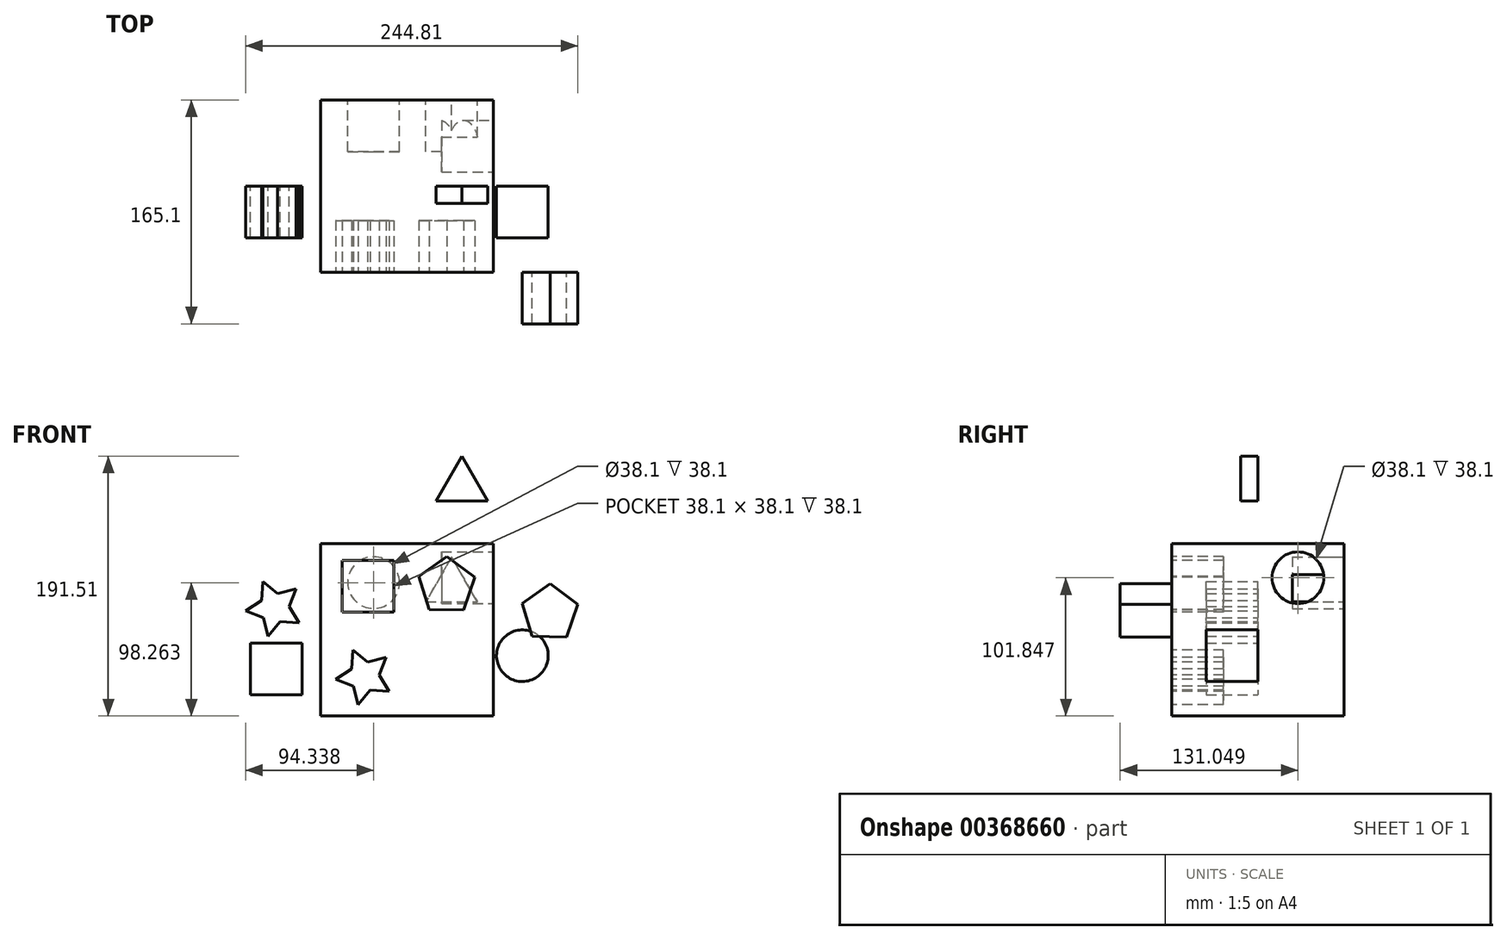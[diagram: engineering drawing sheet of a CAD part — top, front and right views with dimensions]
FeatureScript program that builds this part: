
annotation { "Feature Type Name" : "Feature", "Feature Type Description" : "" }
export const myFeature = defineFeature(function(context is Context, id is Id, definition is map)
    precondition{}
    {
        {
            var Q0;
            Q0=qCreatedBy(makeId("Front.planeOp"),FACE);
            var sketch = newSketch(context, id + "F0", { "sketchPlane" : qUnion([Q0])});
            skLineSegment(sketch, "E0.bottom", {"start": v(63.5, 63.5) * mm, "end": v(-63.5, 63.5) * mm});
            skLineSegment(sketch, "E0.top", {"start": v(63.5, -63.5) * mm, "end": v(-63.5, -63.5) * mm});
            skLineSegment(sketch, "E0.left", {"start": v(63.5, 63.5) * mm, "end": v(63.5, -63.5) * mm});
            skLineSegment(sketch, "E0.right", {"start": v(-63.5, 63.5) * mm, "end": v(-63.5, -63.5) * mm});
            skPoint(sketch, "E0.middle", {"position": v(0, 0) * mm});
            skSolve(sketch);
        }
        {
            var Q0;
            Q0 = qSketchRegion(id + "F0", true);
            extrude(context, id + "F1", {"entities" : qUnion([Q0]), "endBound" : BoundingType.SYMMETRIC, "depth" : 127 * mm});
        }
        {
            var Q0;
            Q0=makeQuery(id+"F1.opExtrude","CAP_FACE",FACE,{"disambiguationData":[OSD([sQuery(id+"F0.wireOp",EDGE,"E0.bottom"),sQuery(id+"F0.wireOp",EDGE,"E0.top"),sQuery(id+"F0.wireOp",EDGE,"E0.left"),sQuery(id+"F0.wireOp",EDGE,"E0.right")])],"isStart":false});
            var sketch = newSketch(context, id + "F2", { "sketchPlane" : qUnion([Q0])});
            skLineSegment(sketch, "E1.bottom", {"start": v(-47.79, 51.24) * mm, "end": v(-9.69, 51.24) * mm});
            skLineSegment(sketch, "E1.top", {"start": v(-47.79, 13.14) * mm, "end": v(-9.69, 13.14) * mm});
            skLineSegment(sketch, "E1.left", {"start": v(-47.79, 51.24) * mm, "end": v(-47.79, 13.14) * mm});
            skLineSegment(sketch, "E1.right", {"start": v(-9.69, 51.24) * mm, "end": v(-9.69, 13.14) * mm});
            skLineSegment(sketch, "E2.bottom", {"start": v(67.2, 12.11) * mm, "end": v(105.3, 12.11) * mm});
            skLineSegment(sketch, "E2.top", {"start": v(67.2, -25.99) * mm, "end": v(105.3, -25.99) * mm});
            skLineSegment(sketch, "E2.left", {"start": v(67.2, 12.11) * mm, "end": v(67.2, -25.99) * mm});
            skLineSegment(sketch, "E2.right", {"start": v(105.3, 12.11) * mm, "end": v(105.3, -25.99) * mm});
            skSolve(sketch);
        }
        {
            var Q0;
            Q0 = qSketchRegion(id + "F2", true);
            extrude(context, id + "F3", {"entities" : qUnion([Q0]), "operationType" : NewBodyOperationType.REMOVE, "oppositeDirection" : true, "depth" : 38.1 * mm});
        }
        {
            var Q0;
            Q0=makeQuery(id+"F1.opExtrude","CAP_FACE",FACE,{"disambiguationData":[OSD([sQuery(id+"F0.wireOp",EDGE,"E0.bottom"),sQuery(id+"F0.wireOp",EDGE,"E0.top"),sQuery(id+"F0.wireOp",EDGE,"E0.left"),sQuery(id+"F0.wireOp",EDGE,"E0.right")])],"isStart":false});
            var sketch = newSketch(context, id + "F4", { "sketchPlane" : qUnion([Q0])});
            skCircle(sketch, "E3.cCircle", {"center": v(29.22, 32.27) * mm, "radius": 17.48 * mm, "construction": true});
            skLineSegment(sketch, "E3.0", {"start": v(16.28, 14.97) * mm, "end": v(8.76, 39.23) * mm});
            skLineSegment(sketch, "E3.1", {"start": v(8.76, 39.23) * mm, "end": v(29.52, 53.88) * mm});
            skLineSegment(sketch, "E3.2", {"start": v(29.52, 53.88) * mm, "end": v(49.86, 38.66) * mm});
            skLineSegment(sketch, "E3.3", {"start": v(49.86, 38.66) * mm, "end": v(41.67, 14.62) * mm});
            skLineSegment(sketch, "E3.4", {"start": v(41.67, 14.62) * mm, "end": v(16.28, 14.97) * mm});
            skPoint(sketch, "E3.0.midPoint", {"position": v(12.52, 27.1) * mm});
            skSolve(sketch);
        }
        {
            var Q0;
            Q0 = qSketchRegion(id + "F4", true);
            extrude(context, id + "F5", {"entities" : qUnion([Q0]), "operationType" : NewBodyOperationType.REMOVE, "oppositeDirection" : true, "depth" : 38.1 * mm});
        }
        {
            var Q0;
            Q0=makeQuery(id+"F1.opExtrude","CAP_FACE",FACE,{"disambiguationData":[OSD([sQuery(id+"F0.wireOp",EDGE,"E0.bottom"),sQuery(id+"F0.wireOp",EDGE,"E0.top"),sQuery(id+"F0.wireOp",EDGE,"E0.left"),sQuery(id+"F0.wireOp",EDGE,"E0.right")])],"isStart":true});
            var sketch = newSketch(context, id + "F6", { "sketchPlane" : qUnion([Q0])});
            skCircle(sketch, "E4.cCircle", {"center": v(-32.84, 31.52) * mm, "radius": 11 * mm, "construction": true});
            skLineSegment(sketch, "E4.0", {"start": v(-13.8, 20.52) * mm, "end": v(-51.9, 20.52) * mm});
            skLineSegment(sketch, "E4.1", {"start": v(-51.9, 20.52) * mm, "end": v(-32.84, 53.52) * mm});
            skLineSegment(sketch, "E4.2", {"start": v(-32.84, 53.52) * mm, "end": v(-13.8, 20.52) * mm});
            skPoint(sketch, "E4.0.midPoint", {"position": v(-32.84, 20.52) * mm});
            skSolve(sketch);
        }
        {
            var Q0;
            Q0 = qSketchRegion(id + "F6", true);
            extrude(context, id + "F7", {"entities" : qUnion([Q0]), "operationType" : NewBodyOperationType.REMOVE, "oppositeDirection" : true, "depth" : 38.1 * mm});
        }
        {
            var Q0;
            Q0=makeQuery(id+"F1.opExtrude","CAP_FACE",FACE,{"disambiguationData":[OSD([sQuery(id+"F0.wireOp",EDGE,"E0.bottom"),sQuery(id+"F0.wireOp",EDGE,"E0.top"),sQuery(id+"F0.wireOp",EDGE,"E0.left"),sQuery(id+"F0.wireOp",EDGE,"E0.right")])],"isStart":true});
            var sketch = newSketch(context, id + "F8", { "sketchPlane" : qUnion([Q0])});
            skCircle(sketch, "E5", {"center": v(24.54, 34.76) * mm, "radius": 19.05 * mm});
            skSolve(sketch);
        }
        {
            var Q0;
            Q0 = qSketchRegion(id + "F8", true);
            extrude(context, id + "F9", {"entities" : qUnion([Q0]), "operationType" : NewBodyOperationType.REMOVE, "oppositeDirection" : true, "depth" : 38.1 * mm});
        }
        {
            var Q0;
            Q0=makeQuery(id+"F1.opExtrude","CAP_FACE",FACE,{"disambiguationData":[OSD([sQuery(id+"F0.wireOp",EDGE,"E0.bottom"),sQuery(id+"F0.wireOp",EDGE,"E0.top"),sQuery(id+"F0.wireOp",EDGE,"E0.left"),sQuery(id+"F0.wireOp",EDGE,"E0.right")])],"isStart":false});
            var sketch = newSketch(context, id + "F10", { "sketchPlane" : qUnion([Q0])});
            skPoint(sketch, "E6.0.midPoint", {"position": v(-46.2, -25.61) * mm});
            skLineSegment(sketch, "E7", {"start": v(-40.74, -28.86) * mm, "end": v(-39.78, -14.86) * mm});
            skLineSegment(sketch, "E8", {"start": v(-28.98, -23.83) * mm, "end": v(-39.78, -14.86) * mm});
            skLineSegment(sketch, "E9", {"start": v(-28.98, -23.83) * mm, "end": v(-15.37, -20.41) * mm});
            skLineSegment(sketch, "E10", {"start": v(-15.37, -20.41) * mm, "end": v(-20.56, -33.45) * mm});
            skLineSegment(sketch, "E11", {"start": v(-20.56, -33.45) * mm, "end": v(-13.1, -45.34) * mm});
            skLineSegment(sketch, "E12", {"start": v(-13.1, -45.34) * mm, "end": v(-27.11, -44.43) * mm});
            skLineSegment(sketch, "E13", {"start": v(-27.11, -44.43) * mm, "end": v(-36.12, -55.2) * mm});
            skLineSegment(sketch, "E14", {"start": v(-36.12, -55.2) * mm, "end": v(-39.58, -41.6) * mm});
            skLineSegment(sketch, "E15", {"start": v(-52.6, -36.36) * mm, "end": v(-39.58, -41.6) * mm});
            skLineSegment(sketch, "E16", {"start": v(-40.74, -28.86) * mm, "end": v(-52.6, -36.36) * mm});
            skArc(sketch, "E17.trimOffspring", {"start": v(-17.82, -45.04) * mm, "mid": v(-16.63, -43.2) * mm, "end": v(-15.7, -41.22) * mm, "construction": true});
            skPoint(sketch, "E18.orphan", {"position": v(-36.69, -22.08) * mm});
            skPoint(sketch, "E19.orphan", {"position": v(-44.79, -35.65) * mm});
            skPoint(sketch, "E20.orphan", {"position": v(-34.38, -47.54) * mm});
            skPoint(sketch, "E21.orphan", {"position": v(-19.85, -41.32) * mm});
            skPoint(sketch, "E22.1.end.orphan", {"position": v(-21.28, -25.58) * mm});
            skSolve(sketch);
        }
        {
            var Q0;
            Q0 = qSketchRegion(id + "F10", true);
            extrude(context, id + "F11", {"entities" : qUnion([Q0]), "operationType" : NewBodyOperationType.REMOVE, "oppositeDirection" : true, "depth" : 38.1 * mm});
        }
        {
            var Q0;
            Q0=makeQuery(id+"F1.opExtrude","SWEPT_FACE",FACE,{"disambiguationData":[OSD([sQuery(id+"F0.wireOp",EDGE,"E0.left")])]});
            var sketch = newSketch(context, id + "F12", { "sketchPlane" : qUnion([Q0])});
            skCircle(sketch, "E23", {"center": v(29.45, 38.35) * mm, "radius": 19.05 * mm});
            skSolve(sketch);
        }
        {
            var Q0;
            Q0 = qSketchRegion(id + "F12", true);
            extrude(context, id + "F13", {"entities" : qUnion([Q0]), "operationType" : NewBodyOperationType.REMOVE, "oppositeDirection" : true, "depth" : 38.1 * mm});
        }
        {
            var Q0;
            Q0=makeQuery(id+"F1.opExtrude","CAP_FACE",FACE,{"disambiguationData":[OSD([sQuery(id+"F0.wireOp",EDGE,"E0.bottom"),sQuery(id+"F0.wireOp",EDGE,"E0.top"),sQuery(id+"F0.wireOp",EDGE,"E0.left"),sQuery(id+"F0.wireOp",EDGE,"E0.right")])],"isStart":false});
            var sketch = newSketch(context, id + "F14", { "sketchPlane" : qUnion([Q0])});
            skLineSegment(sketch, "E24.0", {"start": v(92.35, -4.9) * mm, "end": v(84.84, 19.36) * mm});
            skLineSegment(sketch, "E24.1", {"start": v(84.84, 19.36) * mm, "end": v(105.6, 34) * mm});
            skLineSegment(sketch, "E24.2", {"start": v(105.6, 34) * mm, "end": v(125.93, 18.8) * mm});
            skLineSegment(sketch, "E24.3", {"start": v(125.93, 18.8) * mm, "end": v(117.75, -5.25) * mm});
            skLineSegment(sketch, "E24.4", {"start": v(117.75, -5.25) * mm, "end": v(92.35, -4.9) * mm});
            skSolve(sketch);
        }
        {
            var Q0;
            Q0=makeQuery(id+"F14.imprint","IMPRINT",FACE,{"disambiguationData":[TD([[makeQuery(id+"F14.imprint","IMPRINT",EDGE,{"derivedFrom":sQuery(id+"F14.wireOp",EDGE,"E24.0")}),-1.0]])]});
            extrude(context, id + "F15", {"entities" : qUnion([Q0]), "depth" : 38.1 * mm});
        }
        {
            var Q0;
            Q0=qCreatedBy(makeId("Front.planeOp"),FACE);
            var sketch = newSketch(context, id + "F16", { "sketchPlane" : qUnion([Q0])});
            skLineSegment(sketch, "E25.bottom", {"start": v(-115.44, -9.78) * mm, "end": v(-77.34, -9.78) * mm});
            skLineSegment(sketch, "E25.top", {"start": v(-115.44, -47.88) * mm, "end": v(-77.34, -47.88) * mm});
            skLineSegment(sketch, "E25.left", {"start": v(-115.44, -9.78) * mm, "end": v(-115.44, -47.88) * mm});
            skLineSegment(sketch, "E25.right", {"start": v(-77.34, -9.78) * mm, "end": v(-77.34, -47.88) * mm});
            skSolve(sketch);
        }
        {
            var Q0;
            Q0 = qSketchRegion(id + "F16", true);
            extrude(context, id + "F17", {"entities" : qUnion([Q0]), "depth" : 38.1 * mm});
        }
        {
            var Q0;
            Q0=qCreatedBy(makeId("Front.planeOp"),FACE);
            var sketch = newSketch(context, id + "F18", { "sketchPlane" : qUnion([Q0])});
            skCircle(sketch, "E26", {"center": v(85.07, -19.1) * mm, "radius": 19.05 * mm});
            skSolve(sketch);
        }
        {
            var Q0;
            Q0 = qSketchRegion(id + "F18", true);
            extrude(context, id + "F19", {"entities" : qUnion([Q0]), "depth" : 38.1 * mm});
        }
        {
            var Q0;
            Q0=qCreatedBy(makeId("Front.planeOp"),FACE);
            var sketch = newSketch(context, id + "F20", { "sketchPlane" : qUnion([Q0])});
            skLineSegment(sketch, "E27", {"start": v(-107.02, 21.61) * mm, "end": v(-106.06, 35.61) * mm});
            skLineSegment(sketch, "E28", {"start": v(-95.27, 26.65) * mm, "end": v(-106.06, 35.61) * mm});
            skLineSegment(sketch, "E29", {"start": v(-95.27, 26.65) * mm, "end": v(-81.65, 30.06) * mm});
            skLineSegment(sketch, "E30", {"start": v(-81.65, 30.06) * mm, "end": v(-86.84, 17.02) * mm});
            skLineSegment(sketch, "E31", {"start": v(-86.84, 17.02) * mm, "end": v(-79.39, 5.13) * mm});
            skLineSegment(sketch, "E32", {"start": v(-79.39, 5.13) * mm, "end": v(-93.4, 6.04) * mm});
            skLineSegment(sketch, "E33", {"start": v(-93.4, 6.04) * mm, "end": v(-102.4, -4.72) * mm});
            skLineSegment(sketch, "E34", {"start": v(-102.4, -4.72) * mm, "end": v(-105.86, 8.88) * mm});
            skLineSegment(sketch, "E35", {"start": v(-118.88, 14.11) * mm, "end": v(-105.86, 8.88) * mm});
            skLineSegment(sketch, "E36", {"start": v(-107.02, 21.61) * mm, "end": v(-118.88, 14.11) * mm});
            skSolve(sketch);
        }
        {
            var Q0;
            Q0 = qSketchRegion(id + "F20", true);
            extrude(context, id + "F21", {"entities" : qUnion([Q0]), "depth" : 38.1 * mm});
        }
        {
            var Q0;
            Q0=qCreatedBy(makeId("Front.planeOp"),FACE);
            var sketch = newSketch(context, id + "F22", { "sketchPlane" : qUnion([Q0])});
            skLineSegment(sketch, "E37.0", {"start": v(59.64, 95.01) * mm, "end": v(21.54, 95.01) * mm});
            skLineSegment(sketch, "E37.1", {"start": v(21.54, 95.01) * mm, "end": v(40.6, 128.01) * mm});
            skLineSegment(sketch, "E37.2", {"start": v(40.6, 128.01) * mm, "end": v(59.64, 95.01) * mm});
            skSolve(sketch);
        }
        {
            var Q0;
            Q0 = qConstructionFilter(qBodyType(qCreatedBy(id + "F22" ,EDGE), BodyType.WIRE), ConstructionObject.NO);
            extrude(context, id + "F23", {"bodyType" : ToolBodyType.SURFACE, "surfaceEntities" : qUnion([Q0]), "depth" : 25.4 * mm});
        }
        {
            var Q0;
            Q0 = qSketchRegion(id + "F22", true);
            extrude(context, id + "F24", {"entities" : qUnion([Q0]), "depth" : 12.7 * mm});
        }
    });
